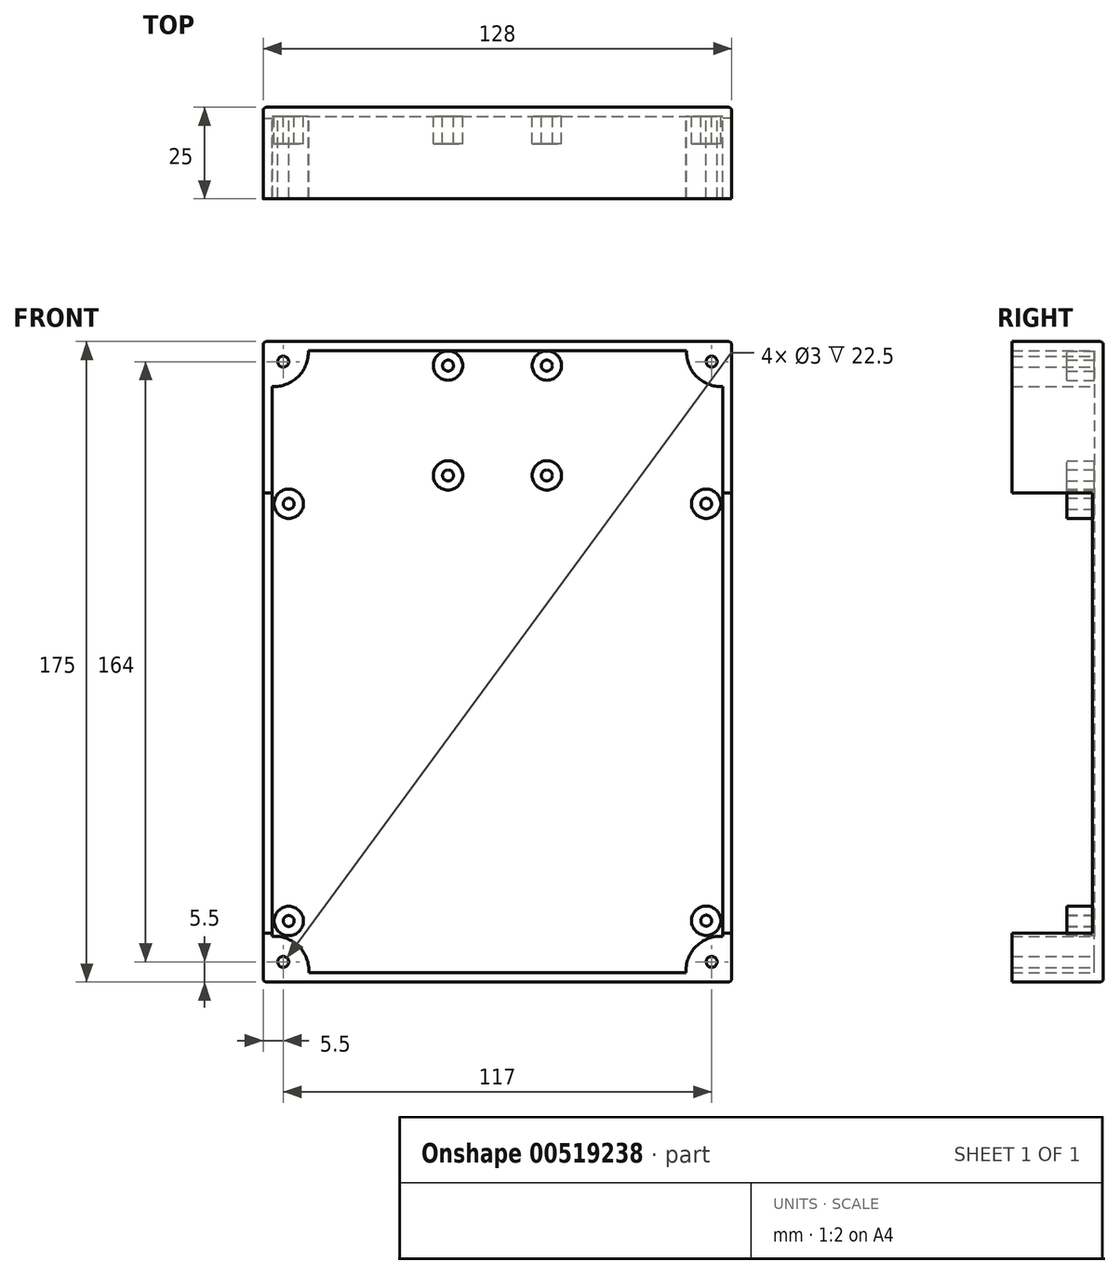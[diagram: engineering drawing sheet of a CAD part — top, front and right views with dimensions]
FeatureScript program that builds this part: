
annotation { "Feature Type Name" : "Feature", "Feature Type Description" : "" }
export const myFeature = defineFeature(function(context is Context, id is Id, definition is map)
    precondition{}
    {
        {
            var Q0;
            Q0=qCreatedBy(makeId("Front.planeOp"),FACE);
            var sketch = newSketch(context, id + "F0", { "sketchPlane" : qUnion([Q0])});
            skLineSegment(sketch, "E0.bottom", {"start": v(-60, 82.67) * mm, "end": v(60, 82.67) * mm});
            skLineSegment(sketch, "E0.top", {"start": v(-60, -37.33) * mm, "end": v(60, -37.33) * mm});
            skLineSegment(sketch, "E0.left", {"start": v(-60, 82.67) * mm, "end": v(-60, -37.33) * mm});
            skLineSegment(sketch, "E0.right", {"start": v(60, 82.67) * mm, "end": v(60, -37.33) * mm});
            skPoint(sketch, "E0.middle", {"position": v(0, 22.67) * mm});
            skLineSegment(sketch, "E1.bottom", {"start": v(-31, 120.13) * mm, "end": v(31, 120.13) * mm});
            skLineSegment(sketch, "E1.top", {"start": v(-31, 84.63) * mm, "end": v(31, 84.63) * mm});
            skLineSegment(sketch, "E1.left", {"start": v(-31, 120.13) * mm, "end": v(-31, 84.63) * mm});
            skLineSegment(sketch, "E1.right", {"start": v(31, 120.13) * mm, "end": v(31, 84.63) * mm});
            skSolve(sketch);
        }
        {
            var Q0;
            Q0=qCreatedBy(makeId("Front.planeOp"),FACE);
            var sketch = newSketch(context, id + "F1", { "sketchPlane" : qUnion([Q0])});
            skLineSegment(sketch, "E2.bottom", {"start": v(-64, 124) * mm, "end": v(64, 124) * mm});
            skLineSegment(sketch, "E2.top", {"start": v(-64, -51) * mm, "end": v(64, -51) * mm});
            skLineSegment(sketch, "E2.left", {"start": v(-64, 124) * mm, "end": v(-64, -51) * mm});
            skLineSegment(sketch, "E2.right", {"start": v(64, 124) * mm, "end": v(64, -51) * mm});
            skPoint(sketch, "E2.middle", {"position": v(0, 36.5) * mm});
            skSolve(sketch);
        }
        {
            var Q0;
            Q0 = qSketchRegion(id + "F1", true);
            extrude(context, id + "F2", {"entities" : qUnion([Q0]), "depth" : 25 * mm, "offsetDistance" : 25 * mm});
        }
        {
            var Q0;
            Q0=makeQuery(id+"F2.opExtrude","CAP_FACE",FACE,{"disambiguationData":[OSD([sQuery(id+"F1.wireOp",EDGE,"E2.bottom"),sQuery(id+"F1.wireOp",EDGE,"E2.top"),sQuery(id+"F1.wireOp",EDGE,"E2.left"),sQuery(id+"F1.wireOp",EDGE,"E2.right")])],"isStart":false});
            shell(context, id + "F3", {"entities" : qUnion([Q0]), "thickness" : 2.5 * mm});
        }
        {
            var Q0;
            Q0=qCreatedBy(makeId("Front.planeOp"),FACE);
            var sketch = newSketch(context, id + "F4", { "sketchPlane" : qUnion([Q0])});
            skCircle(sketch, "E3", {"center": v(-57, 79.67) * mm, "radius": 4 * mm});
            skCircle(sketch, "E4.MirrorC", {"center": v(57, 79.67) * mm, "radius": 4 * mm});
            skCircle(sketch, "E5.MirrorC", {"center": v(57, -34.25) * mm, "radius": 4 * mm});
            skCircle(sketch, "E6.MirrorC", {"center": v(-57, -34.33) * mm, "radius": 4 * mm});
            skCircle(sketch, "E7", {"center": v(-57, 79.67) * mm, "radius": 1.5 * mm});
            skCircle(sketch, "E8", {"center": v(57, 79.67) * mm, "radius": 1.5 * mm});
            skCircle(sketch, "E9", {"center": v(57, -34.25) * mm, "radius": 1.5 * mm});
            skCircle(sketch, "E10", {"center": v(-57, -34.33) * mm, "radius": 1.5 * mm});
            skCircle(sketch, "E11", {"center": v(-13.5, 117.41) * mm, "radius": 4 * mm});
            skCircle(sketch, "E12", {"center": v(-13.5, 117.41) * mm, "radius": 1.5 * mm});
            skCircle(sketch, "E13", {"center": v(13.5, 117.41) * mm, "radius": 4 * mm});
            skCircle(sketch, "E14", {"center": v(13.5, 117.41) * mm, "radius": 1.5 * mm});
            skCircle(sketch, "E15", {"center": v(-13.5, 87.41) * mm, "radius": 4 * mm});
            skCircle(sketch, "E16", {"center": v(-13.5, 87.41) * mm, "radius": 1.5 * mm});
            skCircle(sketch, "E17", {"center": v(13.5, 87.41) * mm, "radius": 4 * mm});
            skCircle(sketch, "E18", {"center": v(13.5, 87.41) * mm, "radius": 1.5 * mm});
            skSolve(sketch);
        }
        {
            var Q0;
            Q0 = qSketchRegion(id + "F4", true);
            extrude(context, id + "F5", {"entities" : qUnion([Q0]), "operationType" : NewBodyOperationType.ADD, "depth" : 10 * mm, "offsetDistance" : 25 * mm});
        }
        {
            var Q0;
            Q0=qCreatedBy(makeId("Front.planeOp"),FACE);
            cPlane(context, id + "F6", {"entities" : qUnion([Q0]), "cplaneType" : CPlaneType.OFFSET, "offset" : 3 * mm, "width" : 150 * mm, "height" : 150 * mm});
        }
        {
            var Q0;
            Q0=qCreatedBy(id+"F6.planeOp",FACE);
            var sketch = newSketch(context, id + "F7", { "sketchPlane" : qUnion([Q0])});
            skLineSegment(sketch, "E19.bottom", {"start": v(-68.21, 82.67) * mm, "end": v(-61.25, 82.67) * mm});
            skLineSegment(sketch, "E19.top", {"start": v(-68.21, -37.67) * mm, "end": v(-61.25, -37.67) * mm});
            skLineSegment(sketch, "E19.left", {"start": v(-68.21, 82.67) * mm, "end": v(-68.21, -37.67) * mm});
            skLineSegment(sketch, "E19.right", {"start": v(-61.25, 82.67) * mm, "end": v(-61.25, -37.67) * mm});
            skPoint(sketch, "E19.middle", {"position": v(-64.73, 22.5) * mm});
            skLineSegment(sketch, "E20.MirrorCS", {"start": v(68.21, 82.67) * mm, "end": v(68.21, -37.67) * mm});
            skLineSegment(sketch, "E21.MirrorCS", {"start": v(68.21, 82.67) * mm, "end": v(61.25, 82.67) * mm});
            skLineSegment(sketch, "E22.MirrorCS", {"start": v(61.25, 82.67) * mm, "end": v(61.25, -37.67) * mm});
            skLineSegment(sketch, "E23.MirrorCS", {"start": v(68.21, -37.67) * mm, "end": v(61.25, -37.67) * mm});
            skSolve(sketch);
        }
        {
            var Q0;
            Q0 = qSketchRegion(id + "F7", true);
            extrude(context, id + "F8", {"entities" : qUnion([Q0]), "operationType" : NewBodyOperationType.REMOVE, "depth" : 35 * mm, "offsetDistance" : 25 * mm});
        }
        {
            var Q0;
            Q0=qCreatedBy(makeId("Front.planeOp"),FACE);
            var sketch = newSketch(context, id + "F9", { "sketchPlane" : qUnion([Q0])});
            skLineSegment(sketch, "E24.bottom", {"start": v(-61.5, -48.5) * mm, "end": v(-61.5, -38.5) * mm});
            skLineSegment(sketch, "E24.left", {"start": v(-61.5, -48.5) * mm, "end": v(-51.5, -48.5) * mm});
            skArc(sketch, "E25", {"start": v(-51.5, -48.5) * mm, "mid": v(-54.26, -41.26) * mm, "end": v(-61.5, -38.5) * mm});
            skArc(sketch, "E26.MirrorCS", {"start": v(51.5, -48.5) * mm, "mid": v(54.26, -41.26) * mm, "end": v(61.5, -38.5) * mm});
            skLineSegment(sketch, "E27.MirrorCS", {"start": v(61.5, -48.5) * mm, "end": v(51.5, -48.5) * mm});
            skLineSegment(sketch, "E28.MirrorCS", {"start": v(61.5, -48.5) * mm, "end": v(61.5, -38.5) * mm});
            skCircle(sketch, "E29", {"center": v(-58.5, 118.5) * mm, "radius": 1.5 * mm});
            skCircle(sketch, "E30.MirrorC", {"center": v(58.5, 118.5) * mm, "radius": 1.5 * mm});
            skCircle(sketch, "E31", {"center": v(-58.5, -45.5) * mm, "radius": 1.5 * mm});
            skCircle(sketch, "E32.MirrorC", {"center": v(58.5, -45.5) * mm, "radius": 1.5 * mm});
            skArc(sketch, "E33.MirrorCS", {"start": v(-51.65, 121.68) * mm, "mid": v(-54.4, 114.44) * mm, "end": v(-61.65, 111.68) * mm});
            skLineSegment(sketch, "E34.MirrorCS", {"start": v(-61.65, 121.68) * mm, "end": v(-51.65, 121.68) * mm});
            skLineSegment(sketch, "E35.MirrorCS", {"start": v(-61.65, 121.68) * mm, "end": v(-61.65, 111.68) * mm});
            skLineSegment(sketch, "E36.MirrorCS", {"start": v(61.65, 121.68) * mm, "end": v(51.65, 121.68) * mm});
            skLineSegment(sketch, "E37.MirrorCS", {"start": v(61.65, 121.68) * mm, "end": v(61.65, 111.68) * mm});
            skArc(sketch, "E38.MirrorCS", {"start": v(51.65, 121.68) * mm, "mid": v(54.4, 114.44) * mm, "end": v(61.65, 111.68) * mm});
            skSolve(sketch);
        }
        {
            var Q0;
            Q0 = qSketchRegion(id + "F9", true);
            extrude(context, id + "F10", {"entities" : qUnion([Q0]), "operationType" : NewBodyOperationType.ADD, "depth" : 25 * mm, "offsetDistance" : 25 * mm});
        }
        {
            var Q0;
            Q0=makeQuery(id+"F2.opExtrude","SWEPT_EDGE",EDGE,{"disambiguationData":[OSD([sQuery(id+"F1.wireOp",EDGE,"E2.bottom"),sQuery(id+"F1.wireOp",EDGE,"E2.left")])]});
            var Q1;
            Q1=makeQuery(id+"F2.opExtrude","SWEPT_EDGE",EDGE,{"disambiguationData":[OSD([sQuery(id+"F1.wireOp",EDGE,"E2.bottom"),sQuery(id+"F1.wireOp",EDGE,"E2.right")])]});
            var Q2;
            Q2=makeQuery(id+"F2.opExtrude","CAP_EDGE",EDGE,{"disambiguationData":[OSD([sQuery(id+"F1.wireOp",EDGE,"E2.bottom")])],"isStart":true});
            var Q3;
            Q3=makeQuery(id+"F2.opExtrude","CAP_EDGE",EDGE,{"disambiguationData":[OSD([sQuery(id+"F1.wireOp",EDGE,"E2.right")])],"isStart":true});
            var Q4;
            Q4=makeQuery(id+"F2.opExtrude","CAP_EDGE",EDGE,{"disambiguationData":[OSD([sQuery(id+"F1.wireOp",EDGE,"E2.top")])],"isStart":true});
            var Q5;
            Q5=makeQuery(id+"F2.opExtrude","SWEPT_EDGE",EDGE,{"disambiguationData":[OSD([sQuery(id+"F1.wireOp",EDGE,"E2.top"),sQuery(id+"F1.wireOp",EDGE,"E2.right")])]});
            var Q6;
            Q6=makeQuery(id+"F2.opExtrude","SWEPT_EDGE",EDGE,{"disambiguationData":[OSD([sQuery(id+"F1.wireOp",EDGE,"E2.top"),sQuery(id+"F1.wireOp",EDGE,"E2.left")])]});
            var Q7;
            Q7=makeQuery(id+"F2.opExtrude","CAP_EDGE",EDGE,{"disambiguationData":[OSD([sQuery(id+"F1.wireOp",EDGE,"E2.left")])],"isStart":true});
            fillet(context, id + "F11", {"entities" : qUnion([Q0, Q1, Q2, Q3, Q4, Q5, Q6, Q7]), "radius" : 1 * mm, "tangentPropagation" : true, "allowEdgeOverflow" : false});
        }
    });
